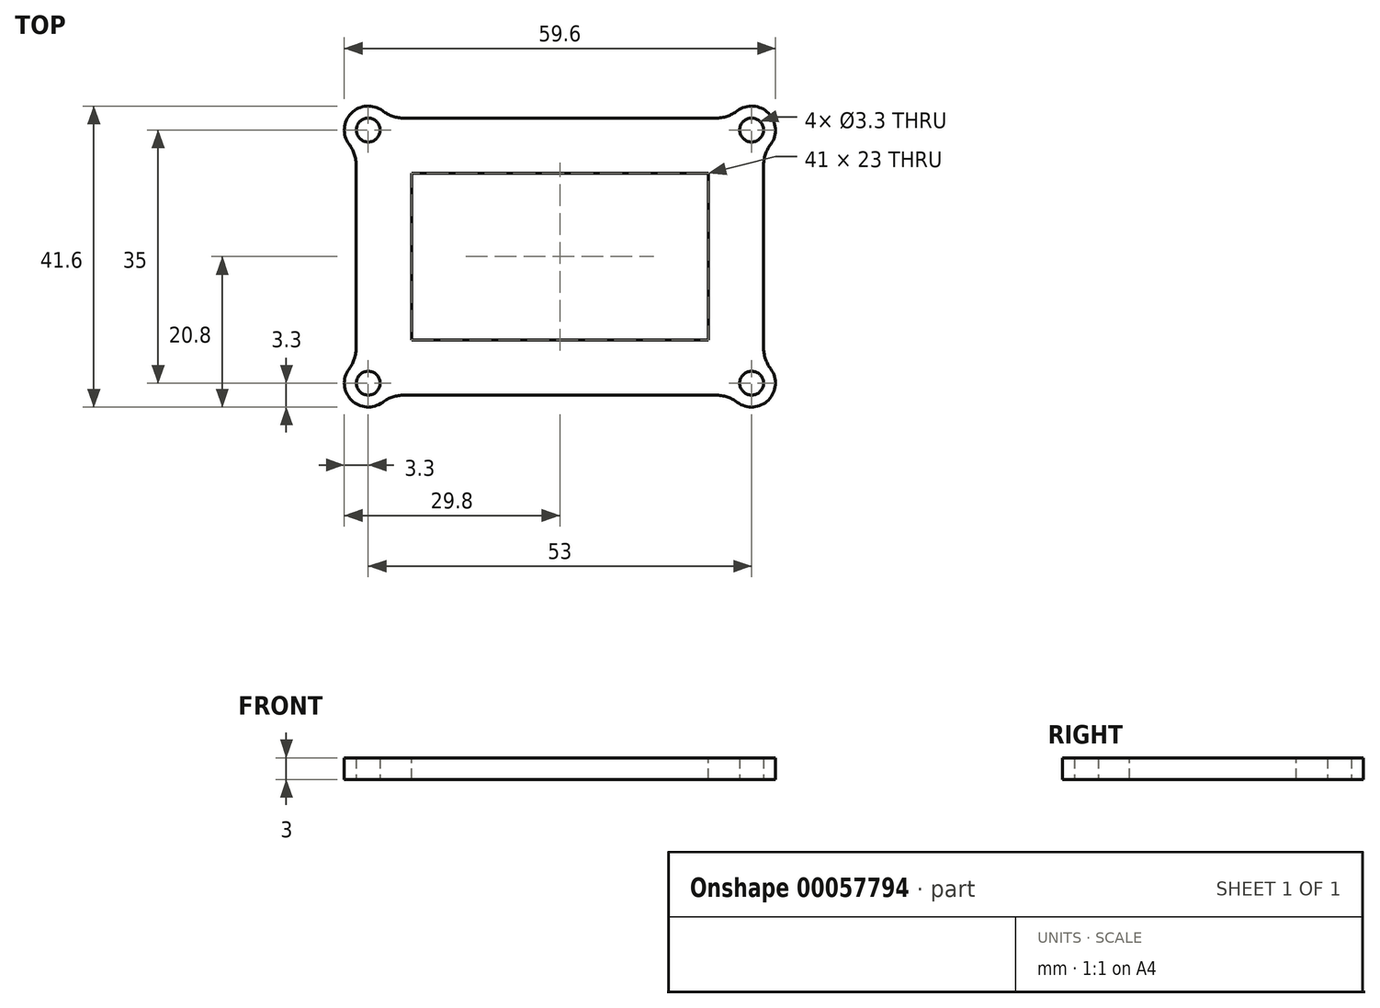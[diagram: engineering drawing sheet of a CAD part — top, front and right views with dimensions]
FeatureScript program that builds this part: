
annotation { "Feature Type Name" : "Feature", "Feature Type Description" : "" }
export const myFeature = defineFeature(function(context is Context, id is Id, definition is map)
    precondition{}
    {
        {
            var Q0;
            Q0=qCreatedBy(makeId("Top.planeOp"),FACE);
            var sketch = newSketch(context, id + "F0", { "sketchPlane" : qUnion([Q0])});
            skLineSegment(sketch, "E0", {"start": v(0, 0) * mm, "end": v(0, 49.8) * mm, "construction": true});
            skLineSegment(sketch, "E1.0", {"start": v(23.5, 0) * mm, "end": v(23.5, 29) * mm});
            skLineSegment(sketch, "E2.0", {"start": v(-23.5, 0) * mm, "end": v(-23.5, 29) * mm});
            skLineSegment(sketch, "E3", {"start": v(-23.5, 0) * mm, "end": v(23.5, 0) * mm});
            skLineSegment(sketch, "E4.0", {"start": v(-23.5, 29) * mm, "end": v(23.5, 29) * mm});
            skLineSegment(sketch, "E5.0", {"start": v(-26.5, 0) * mm, "end": v(-26.5, 33.65) * mm, "construction": true});
            skLineSegment(sketch, "E6.0", {"start": v(-26.5, 32) * mm, "end": v(30.75, 32) * mm, "construction": true});
            skLineSegment(sketch, "E7.0", {"start": v(26.5, 0) * mm, "end": v(26.5, 32) * mm, "construction": true});
            skLineSegment(sketch, "E8.0", {"start": v(-23.5, -3) * mm, "end": v(23.5, -3) * mm, "construction": true});
            skCircle(sketch, "E9", {"center": v(-26.5, 32) * mm, "radius": 1.65 * mm});
            skArc(sketch, "E10", {"start": v(-24.53, 34.64) * mm, "mid": v(-28.83, 34.33) * mm, "end": v(-29.14, 30.02) * mm});
            skArc(sketch, "E11.MirrorC", {"start": v(24.53, 34.64) * mm, "mid": v(28.83, 34.33) * mm, "end": v(29.14, 30.02) * mm});
            skCircle(sketch, "E12.MirrorC", {"center": v(26.5, 32) * mm, "radius": 1.65 * mm});
            skLineSegment(sketch, "E13", {"start": v(-21.53, 33.65) * mm, "end": v(21.53, 33.65) * mm});
            skLineSegment(sketch, "E14", {"start": v(-23.5, 14.5) * mm, "end": v(23.5, 14.5) * mm, "construction": true});
            skArc(sketch, "E15.MirrorC", {"start": v(-27.35, -6.19) * mm, "mid": v(-29.62, -4.08) * mm, "end": v(-29.14, -1.02) * mm});
            skCircle(sketch, "E16.MirrorC", {"center": v(-26.5, -3) * mm, "radius": 1.65 * mm});
            skArc(sketch, "E17.MirrorC", {"start": v(27.35, -6.19) * mm, "mid": v(29.62, -4.08) * mm, "end": v(29.14, -1.02) * mm});
            skCircle(sketch, "E18.MirrorC", {"center": v(26.5, -3) * mm, "radius": 1.65 * mm});
            skLineSegment(sketch, "E19", {"start": v(-28.15, 32.12) * mm, "end": v(-28.15, 31.88) * mm});
            skLineSegment(sketch, "E20.MirrorCS", {"start": v(28.15, 32.12) * mm, "end": v(28.15, 31.88) * mm});
            skLineSegment(sketch, "E21.trimOffspring", {"start": v(-28.15, 27.03) * mm, "end": v(-28.15, 1.97) * mm});
            skPoint(sketch, "E22.orphan", {"position": v(-28.15, -2.88) * mm});
            skPoint(sketch, "E23.orphan", {"position": v(28.15, -2.88) * mm});
            skLineSegment(sketch, "E24.trimOffspring", {"start": v(28.15, 27.03) * mm, "end": v(28.15, 1.97) * mm});
            skPoint(sketch, "E25.visualSharp", {"position": v(-28.15, 29.14) * mm});
            skArc(sketch, "E25.filletArc", {"start": v(-28.15, 27.03) * mm, "mid": v(-28.4, 28.6) * mm, "end": v(-29.14, 30.02) * mm});
            skPoint(sketch, "E26.visualSharp", {"position": v(-28.15, -0.14) * mm});
            skArc(sketch, "E26.filletArc", {"start": v(-29.14, -1.02) * mm, "mid": v(-28.4, 0.4) * mm, "end": v(-28.15, 1.97) * mm});
            skPoint(sketch, "E27.visualSharp", {"position": v(-23.64, 33.65) * mm});
            skArc(sketch, "E27.filletArc", {"start": v(-24.53, 34.64) * mm, "mid": v(-23.1, 33.9) * mm, "end": v(-21.53, 33.65) * mm});
            skPoint(sketch, "E28.visualSharp", {"position": v(23.64, 33.65) * mm});
            skArc(sketch, "E28.filletArc", {"start": v(21.53, 33.65) * mm, "mid": v(23.1, 33.9) * mm, "end": v(24.53, 34.64) * mm});
            skPoint(sketch, "E29.visualSharp", {"position": v(28.15, 29.14) * mm});
            skArc(sketch, "E29.filletArc", {"start": v(29.14, 30.02) * mm, "mid": v(28.4, 28.6) * mm, "end": v(28.15, 27.03) * mm});
            skPoint(sketch, "E30.visualSharp", {"position": v(28.15, -0.14) * mm});
            skArc(sketch, "E30.filletArc", {"start": v(28.15, 1.97) * mm, "mid": v(28.4, 0.4) * mm, "end": v(29.14, -1.02) * mm});
            skPoint(sketch, "E31.visualSharp", {"position": v(23.64, -4.65) * mm});
            skLineSegment(sketch, "E32.MirrorCS", {"start": v(-21.53, -4.65) * mm, "end": v(21.53, -4.65) * mm});
            skArc(sketch, "E33", {"start": v(-29.14, -1.02) * mm, "mid": v(-28.83, -5.33) * mm, "end": v(-24.53, -5.64) * mm});
            skPoint(sketch, "E34.orphan", {"position": v(-21.53, -4.65) * mm});
            skPoint(sketch, "E35.visualSharp", {"position": v(-23.64, -4.65) * mm});
            skArc(sketch, "E35.filletArc", {"start": v(-21.53, -4.65) * mm, "mid": v(-23.1, -4.9) * mm, "end": v(-24.53, -5.64) * mm});
            skArc(sketch, "E36.MirrorCS", {"start": v(29.14, -1.02) * mm, "mid": v(28.83, -5.33) * mm, "end": v(24.53, -5.64) * mm});
            skArc(sketch, "E37.MirrorCS", {"start": v(21.53, -4.65) * mm, "mid": v(23.1, -4.9) * mm, "end": v(24.53, -5.64) * mm});
            skSolve(sketch);
        }
        {
            var Q0;
            Q0=makeQuery(id+"F0.imprint","IMPRINT",FACE,{"disambiguationData":[TD([[makeQuery(id+"F0.imprint","IMPRINT",EDGE,{"derivedFrom":sQuery(id+"F0.wireOp",EDGE,"E1.0")}),1.0]])]});
            extrude(context, id + "F1", {"entities" : qUnion([Q0]), "depth" : 3 * mm});
        }
        {
            var Q0;
            Q0=qSketchRegion(id+"F0",true);
            extrude(context, id + "F2", {"entities" : qUnion([Q0]), "operationType" : NewBodyOperationType.ADD, "depth" : 3 * mm});
        }
        {
            var Q0;
            Q0=makeQuery(id+"F1.opExtrude","CAP_FACE",FACE,{"disambiguationData":[OSD([sQuery(id+"F0.wireOp",EDGE,"E1.0"),sQuery(id+"F0.wireOp",EDGE,"E2.0"),sQuery(id+"F0.wireOp",EDGE,"E3"),sQuery(id+"F0.wireOp",EDGE,"E4.0")])],"isStart":false});
            var sketch = newSketch(context, id + "F3", { "sketchPlane" : qUnion([Q0])});
            skLineSegment(sketch, "E38.bottom", {"start": v(-23.5, 29) * mm, "end": v(23.5, 29) * mm, "construction": true});
            skLineSegment(sketch, "E38.top", {"start": v(-23.5, 0) * mm, "end": v(23.5, 0) * mm, "construction": true});
            skLineSegment(sketch, "E38.left", {"start": v(-23.5, 29) * mm, "end": v(-23.5, 0) * mm, "construction": true});
            skLineSegment(sketch, "E38.right", {"start": v(23.5, 29) * mm, "end": v(23.5, 0) * mm, "construction": true});
            skLineSegment(sketch, "E39.0", {"start": v(-20.5, 26) * mm, "end": v(20.5, 26) * mm});
            skLineSegment(sketch, "E40.0", {"start": v(-20.5, 26) * mm, "end": v(-20.5, 3) * mm});
            skLineSegment(sketch, "E41.0", {"start": v(-20.5, 3) * mm, "end": v(20.5, 3) * mm});
            skLineSegment(sketch, "E42.0", {"start": v(20.5, 26) * mm, "end": v(20.5, 3) * mm});
            skSolve(sketch);
        }
        {
            var Q0;
            Q0=makeQuery(id+"F3.imprint","IMPRINT",FACE,{"disambiguationData":[TD([[makeQuery(id+"F3.imprint","IMPRINT",EDGE,{"derivedFrom":sQuery(id+"F3.wireOp",EDGE,"E39.0")}),-1.0]])]});
            extrude(context, id + "F4", {"entities" : qUnion([Q0]), "operationType" : NewBodyOperationType.REMOVE, "endBound" : BoundingType.THROUGH_ALL, "oppositeDirection" : true, "depth" : 1.5 * mm});
        }
    });
